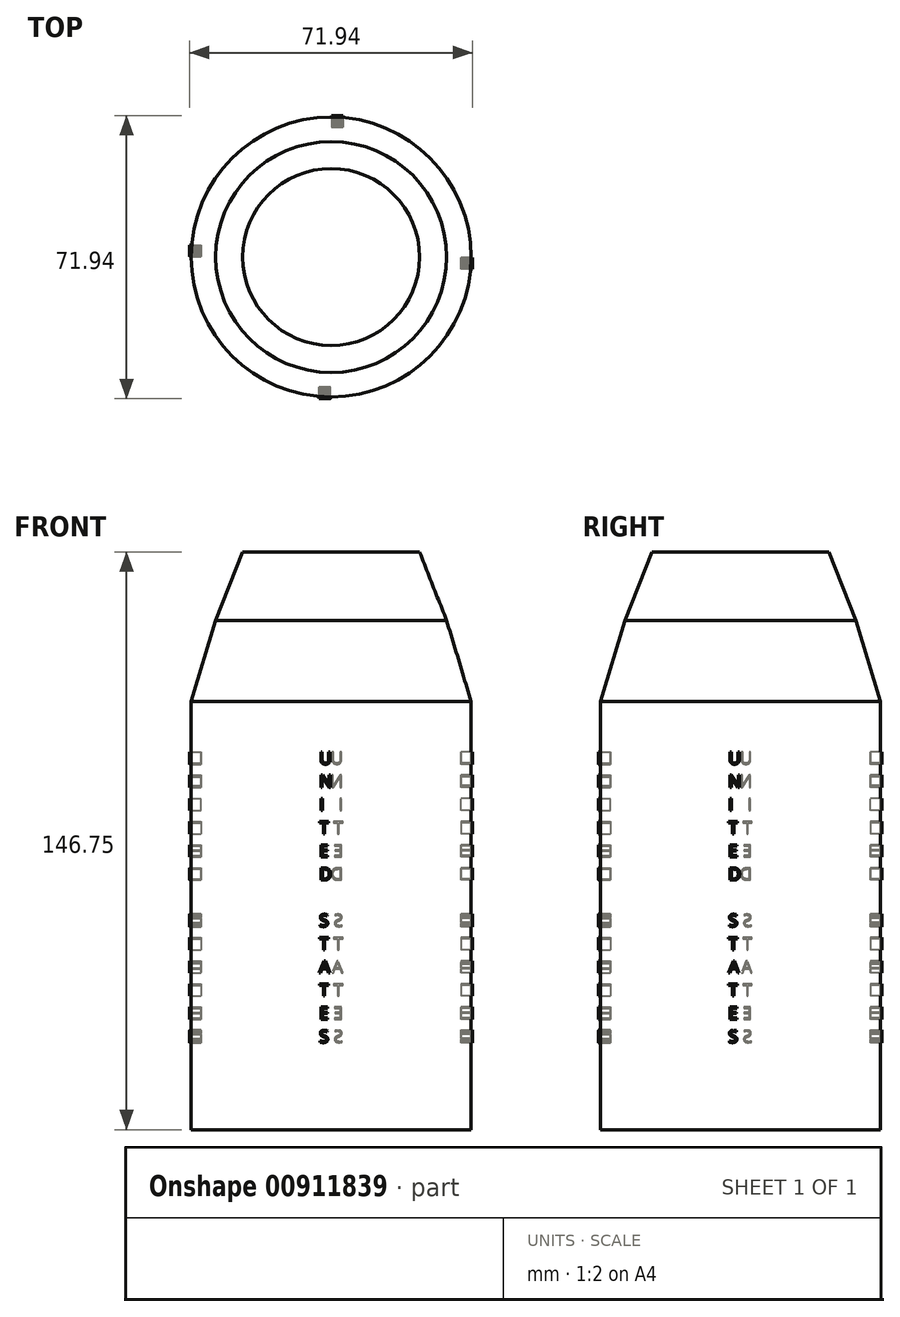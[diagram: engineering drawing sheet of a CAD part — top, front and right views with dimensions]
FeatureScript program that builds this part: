
annotation { "Feature Type Name" : "Feature", "Feature Type Description" : "" }
export const myFeature = defineFeature(function(context is Context, id is Id, definition is map)
    precondition{}
    {
        {
            var Q0;
            Q0=qCreatedBy(makeId("Front.planeOp"),FACE);
            var sketch = newSketch(context, id + "F0", { "sketchPlane" : qUnion([Q0])});
            skLineSegment(sketch, "E0.bottom", {"start": v(0, -75.35) * mm, "end": v(-35.56, -75.35) * mm});
            skLineSegment(sketch, "E0.top", {"start": v(0, 33.49) * mm, "end": v(-35.56, 33.49) * mm});
            skLineSegment(sketch, "E0.left", {"start": v(0, -75.35) * mm, "end": v(0, 33.49) * mm});
            skLineSegment(sketch, "E0.right", {"start": v(-35.56, -75.35) * mm, "end": v(-35.56, 33.49) * mm});
            skLineSegment(sketch, "E1", {"start": v(-35.56, 33.49) * mm, "end": v(-29.33, 53.99) * mm});
            skLineSegment(sketch, "E2", {"start": v(-29.33, 53.99) * mm, "end": v(0, 53.99) * mm});
            skLineSegment(sketch, "E3", {"start": v(0, 53.99) * mm, "end": v(0, 33.49) * mm});
            skLineSegment(sketch, "E4", {"start": v(-29.33, 53.99) * mm, "end": v(-22.49, 71.4) * mm});
            skLineSegment(sketch, "E5", {"start": v(0, 71.4) * mm, "end": v(0, 53.99) * mm});
            skLineSegment(sketch, "E6", {"start": v(0, 85.08) * mm, "end": v(0, -81.57) * mm});
            skLineSegment(sketch, "E7", {"start": v(-22.49, 71.4) * mm, "end": v(0, 71.4) * mm});
            skSolve(sketch);
        }
        {
            var Q0;
            Q0 = qSketchRegion(id + "F0", true);
            var Q1;
            Q1=sQuery(id+"F0.wireOp",EDGE,"E6");
            revolve(context, id + "F1", {"surfaceOperationType" : NewSurfaceOperationType.NEW, "entities" : qUnion([Q0]), "axis" : qUnion([Q1]), "revolveType" : RevolveType.FULL});
        }
        {
            var Q0;
            Q0=qCreatedBy(makeId("Front.planeOp"),FACE);
            cPlane(context, id + "F2", {"entities" : qUnion([Q0]), "cplaneType" : CPlaneType.OFFSET, "offset" : 33.02 * mm, "width" : 152.4 * mm, "height" : 152.4 * mm});
        }
        {
            var Q0;
            Q0=qCreatedBy(id+"F2.planeOp",FACE);
            var sketch = newSketch(context, id + "F3", { "sketchPlane" : qUnion([Q0])});
            skText(sketch, "E8", { "text": "U\nN\nI\nT\nE\nD\n\nS\nT\nA\nT\nE\nS", "fontName": "OpenSans-Regular.ttf"});
            const initialGuessF3  = {"E8": [-0.00302, 0.01752, 1, 0, 0.00312]};
            skSetInitialGuess(sketch, initialGuessF3);
            skSolve(sketch);
        }
        {
            var Q0;
            Q0 = qSketchRegion(id + "F3", true);
            extrude(context, id + "F4", {"entities" : qUnion([Q0]), "depth" : 2.95 * mm, "offsetDistance" : 25.4 * mm});
        }
        {
            var Q0;
            Q0=makeQuery(id+"F4.opExtrude","SWEPT_BODY",BODY,{"disambiguationData":[OSD([sQuery(id+"F3.wireOp",EDGE,"E8.sketch_text.stroke-0"),sQuery(id+"F3.wireOp",EDGE,"E8.sketch_text.stroke-1"),sQuery(id+"F3.wireOp",EDGE,"E8.sketch_text.stroke-2"),sQuery(id+"F3.wireOp",EDGE,"E8.sketch_text.stroke-3"),sQuery(id+"F3.wireOp",EDGE,"E8.sketch_text.stroke-4"),sQuery(id+"F3.wireOp",EDGE,"E8.sketch_text.stroke-5"),sQuery(id+"F3.wireOp",EDGE,"E8.sketch_text.stroke-6"),sQuery(id+"F3.wireOp",EDGE,"E8.sketch_text.stroke-7"),sQuery(id+"F3.wireOp",EDGE,"E8.sketch_text.stroke-8"),sQuery(id+"F3.wireOp",EDGE,"E8.sketch_text.stroke-9"),sQuery(id+"F3.wireOp",EDGE,"E8.sketch_text.stroke-10"),sQuery(id+"F3.wireOp",EDGE,"E8.sketch_text.stroke-11"),sQuery(id+"F3.wireOp",EDGE,"E8.sketch_text.stroke-12"),sQuery(id+"F3.wireOp",EDGE,"E8.sketch_text.stroke-13")])]});
            var Q1;
            Q1=makeQuery(id+"F4.opExtrude","SWEPT_BODY",BODY,{"disambiguationData":[OSD([sQuery(id+"F3.wireOp",EDGE,"E8.sketch_text.stroke-14"),sQuery(id+"F3.wireOp",EDGE,"E8.sketch_text.stroke-15"),sQuery(id+"F3.wireOp",EDGE,"E8.sketch_text.stroke-16"),sQuery(id+"F3.wireOp",EDGE,"E8.sketch_text.stroke-17"),sQuery(id+"F3.wireOp",EDGE,"E8.sketch_text.stroke-18"),sQuery(id+"F3.wireOp",EDGE,"E8.sketch_text.stroke-19"),sQuery(id+"F3.wireOp",EDGE,"E8.sketch_text.stroke-20"),sQuery(id+"F3.wireOp",EDGE,"E8.sketch_text.stroke-21"),sQuery(id+"F3.wireOp",EDGE,"E8.sketch_text.stroke-22"),sQuery(id+"F3.wireOp",EDGE,"E8.sketch_text.stroke-23"),sQuery(id+"F3.wireOp",EDGE,"E8.sketch_text.stroke-24"),sQuery(id+"F3.wireOp",EDGE,"E8.sketch_text.stroke-25"),sQuery(id+"F3.wireOp",EDGE,"E8.sketch_text.stroke-26"),sQuery(id+"F3.wireOp",EDGE,"E8.sketch_text.stroke-27"),sQuery(id+"F3.wireOp",EDGE,"E8.sketch_text.stroke-28")])]});
            var Q2;
            Q2=makeQuery(id+"F4.opExtrude","SWEPT_BODY",BODY,{"disambiguationData":[OSD([sQuery(id+"F3.wireOp",EDGE,"E8.sketch_text.stroke-29"),sQuery(id+"F3.wireOp",EDGE,"E8.sketch_text.stroke-30"),sQuery(id+"F3.wireOp",EDGE,"E8.sketch_text.stroke-31"),sQuery(id+"F3.wireOp",EDGE,"E8.sketch_text.stroke-32")])]});
            var Q3;
            Q3=makeQuery(id+"F4.opExtrude","SWEPT_BODY",BODY,{"disambiguationData":[OSD([sQuery(id+"F3.wireOp",EDGE,"E8.sketch_text.stroke-33"),sQuery(id+"F3.wireOp",EDGE,"E8.sketch_text.stroke-34"),sQuery(id+"F3.wireOp",EDGE,"E8.sketch_text.stroke-35"),sQuery(id+"F3.wireOp",EDGE,"E8.sketch_text.stroke-36"),sQuery(id+"F3.wireOp",EDGE,"E8.sketch_text.stroke-37"),sQuery(id+"F3.wireOp",EDGE,"E8.sketch_text.stroke-38"),sQuery(id+"F3.wireOp",EDGE,"E8.sketch_text.stroke-39"),sQuery(id+"F3.wireOp",EDGE,"E8.sketch_text.stroke-40")])]});
            var Q4;
            Q4=makeQuery(id+"F4.opExtrude","SWEPT_BODY",BODY,{"disambiguationData":[OSD([sQuery(id+"F3.wireOp",EDGE,"E8.sketch_text.stroke-41"),sQuery(id+"F3.wireOp",EDGE,"E8.sketch_text.stroke-42"),sQuery(id+"F3.wireOp",EDGE,"E8.sketch_text.stroke-43"),sQuery(id+"F3.wireOp",EDGE,"E8.sketch_text.stroke-44"),sQuery(id+"F3.wireOp",EDGE,"E8.sketch_text.stroke-45"),sQuery(id+"F3.wireOp",EDGE,"E8.sketch_text.stroke-46"),sQuery(id+"F3.wireOp",EDGE,"E8.sketch_text.stroke-47"),sQuery(id+"F3.wireOp",EDGE,"E8.sketch_text.stroke-48"),sQuery(id+"F3.wireOp",EDGE,"E8.sketch_text.stroke-49"),sQuery(id+"F3.wireOp",EDGE,"E8.sketch_text.stroke-50"),sQuery(id+"F3.wireOp",EDGE,"E8.sketch_text.stroke-51"),sQuery(id+"F3.wireOp",EDGE,"E8.sketch_text.stroke-52")])]});
            var Q5;
            Q5=makeQuery(id+"F4.opExtrude","SWEPT_BODY",BODY,{"disambiguationData":[OSD([sQuery(id+"F3.wireOp",EDGE,"E8.sketch_text.stroke-53"),sQuery(id+"F3.wireOp",EDGE,"E8.sketch_text.stroke-54"),sQuery(id+"F3.wireOp",EDGE,"E8.sketch_text.stroke-55"),sQuery(id+"F3.wireOp",EDGE,"E8.sketch_text.stroke-56"),sQuery(id+"F3.wireOp",EDGE,"E8.sketch_text.stroke-57"),sQuery(id+"F3.wireOp",EDGE,"E8.sketch_text.stroke-58"),sQuery(id+"F3.wireOp",EDGE,"E8.sketch_text.stroke-59"),sQuery(id+"F3.wireOp",EDGE,"E8.sketch_text.stroke-60"),sQuery(id+"F3.wireOp",EDGE,"E8.sketch_text.stroke-61"),sQuery(id+"F3.wireOp",EDGE,"E8.sketch_text.stroke-62"),sQuery(id+"F3.wireOp",EDGE,"E8.sketch_text.stroke-63"),sQuery(id+"F3.wireOp",EDGE,"E8.sketch_text.stroke-64"),sQuery(id+"F3.wireOp",EDGE,"E8.sketch_text.stroke-65"),sQuery(id+"F3.wireOp",EDGE,"E8.sketch_text.stroke-66")])]});
            var Q6;
            Q6=makeQuery(id+"F4.opExtrude","SWEPT_BODY",BODY,{"disambiguationData":[OSD([sQuery(id+"F3.wireOp",EDGE,"E8.sketch_text.stroke-67"),sQuery(id+"F3.wireOp",EDGE,"E8.sketch_text.stroke-68"),sQuery(id+"F3.wireOp",EDGE,"E8.sketch_text.stroke-69"),sQuery(id+"F3.wireOp",EDGE,"E8.sketch_text.stroke-70"),sQuery(id+"F3.wireOp",EDGE,"E8.sketch_text.stroke-71"),sQuery(id+"F3.wireOp",EDGE,"E8.sketch_text.stroke-72"),sQuery(id+"F3.wireOp",EDGE,"E8.sketch_text.stroke-73"),sQuery(id+"F3.wireOp",EDGE,"E8.sketch_text.stroke-74"),sQuery(id+"F3.wireOp",EDGE,"E8.sketch_text.stroke-75"),sQuery(id+"F3.wireOp",EDGE,"E8.sketch_text.stroke-76"),sQuery(id+"F3.wireOp",EDGE,"E8.sketch_text.stroke-77"),sQuery(id+"F3.wireOp",EDGE,"E8.sketch_text.stroke-78"),sQuery(id+"F3.wireOp",EDGE,"E8.sketch_text.stroke-79"),sQuery(id+"F3.wireOp",EDGE,"E8.sketch_text.stroke-80"),sQuery(id+"F3.wireOp",EDGE,"E8.sketch_text.stroke-81"),sQuery(id+"F3.wireOp",EDGE,"E8.sketch_text.stroke-82"),sQuery(id+"F3.wireOp",EDGE,"E8.sketch_text.stroke-83"),sQuery(id+"F3.wireOp",EDGE,"E8.sketch_text.stroke-84"),sQuery(id+"F3.wireOp",EDGE,"E8.sketch_text.stroke-85"),sQuery(id+"F3.wireOp",EDGE,"E8.sketch_text.stroke-86"),sQuery(id+"F3.wireOp",EDGE,"E8.sketch_text.stroke-87"),sQuery(id+"F3.wireOp",EDGE,"E8.sketch_text.stroke-88"),sQuery(id+"F3.wireOp",EDGE,"E8.sketch_text.stroke-89"),sQuery(id+"F3.wireOp",EDGE,"E8.sketch_text.stroke-90"),sQuery(id+"F3.wireOp",EDGE,"E8.sketch_text.stroke-91")])]});
            var Q7;
            Q7=makeQuery(id+"F4.opExtrude","SWEPT_BODY",BODY,{"disambiguationData":[OSD([sQuery(id+"F3.wireOp",EDGE,"E8.sketch_text.stroke-92"),sQuery(id+"F3.wireOp",EDGE,"E8.sketch_text.stroke-93"),sQuery(id+"F3.wireOp",EDGE,"E8.sketch_text.stroke-94"),sQuery(id+"F3.wireOp",EDGE,"E8.sketch_text.stroke-95"),sQuery(id+"F3.wireOp",EDGE,"E8.sketch_text.stroke-96"),sQuery(id+"F3.wireOp",EDGE,"E8.sketch_text.stroke-97"),sQuery(id+"F3.wireOp",EDGE,"E8.sketch_text.stroke-98"),sQuery(id+"F3.wireOp",EDGE,"E8.sketch_text.stroke-99")])]});
            var Q8;
            Q8=makeQuery(id+"F4.opExtrude","SWEPT_BODY",BODY,{"disambiguationData":[OSD([sQuery(id+"F3.wireOp",EDGE,"E8.sketch_text.stroke-100"),sQuery(id+"F3.wireOp",EDGE,"E8.sketch_text.stroke-101"),sQuery(id+"F3.wireOp",EDGE,"E8.sketch_text.stroke-102"),sQuery(id+"F3.wireOp",EDGE,"E8.sketch_text.stroke-103"),sQuery(id+"F3.wireOp",EDGE,"E8.sketch_text.stroke-104"),sQuery(id+"F3.wireOp",EDGE,"E8.sketch_text.stroke-105"),sQuery(id+"F3.wireOp",EDGE,"E8.sketch_text.stroke-106"),sQuery(id+"F3.wireOp",EDGE,"E8.sketch_text.stroke-107"),sQuery(id+"F3.wireOp",EDGE,"E8.sketch_text.stroke-108"),sQuery(id+"F3.wireOp",EDGE,"E8.sketch_text.stroke-109"),sQuery(id+"F3.wireOp",EDGE,"E8.sketch_text.stroke-110"),sQuery(id+"F3.wireOp",EDGE,"E8.sketch_text.stroke-111"),sQuery(id+"F3.wireOp",EDGE,"E8.sketch_text.stroke-112")])]});
            var Q9;
            Q9=makeQuery(id+"F4.opExtrude","SWEPT_BODY",BODY,{"disambiguationData":[OSD([sQuery(id+"F3.wireOp",EDGE,"E8.sketch_text.stroke-113"),sQuery(id+"F3.wireOp",EDGE,"E8.sketch_text.stroke-114"),sQuery(id+"F3.wireOp",EDGE,"E8.sketch_text.stroke-115"),sQuery(id+"F3.wireOp",EDGE,"E8.sketch_text.stroke-116"),sQuery(id+"F3.wireOp",EDGE,"E8.sketch_text.stroke-117"),sQuery(id+"F3.wireOp",EDGE,"E8.sketch_text.stroke-118"),sQuery(id+"F3.wireOp",EDGE,"E8.sketch_text.stroke-119"),sQuery(id+"F3.wireOp",EDGE,"E8.sketch_text.stroke-120")])]});
            var Q10;
            Q10=makeQuery(id+"F4.opExtrude","SWEPT_BODY",BODY,{"disambiguationData":[OSD([sQuery(id+"F3.wireOp",EDGE,"E8.sketch_text.stroke-121"),sQuery(id+"F3.wireOp",EDGE,"E8.sketch_text.stroke-122"),sQuery(id+"F3.wireOp",EDGE,"E8.sketch_text.stroke-123"),sQuery(id+"F3.wireOp",EDGE,"E8.sketch_text.stroke-124"),sQuery(id+"F3.wireOp",EDGE,"E8.sketch_text.stroke-125"),sQuery(id+"F3.wireOp",EDGE,"E8.sketch_text.stroke-126"),sQuery(id+"F3.wireOp",EDGE,"E8.sketch_text.stroke-127"),sQuery(id+"F3.wireOp",EDGE,"E8.sketch_text.stroke-128"),sQuery(id+"F3.wireOp",EDGE,"E8.sketch_text.stroke-129"),sQuery(id+"F3.wireOp",EDGE,"E8.sketch_text.stroke-130"),sQuery(id+"F3.wireOp",EDGE,"E8.sketch_text.stroke-131"),sQuery(id+"F3.wireOp",EDGE,"E8.sketch_text.stroke-132")])]});
            var Q11;
            Q11=makeQuery(id+"F4.opExtrude","SWEPT_BODY",BODY,{"disambiguationData":[OSD([sQuery(id+"F3.wireOp",EDGE,"E8.sketch_text.stroke-133"),sQuery(id+"F3.wireOp",EDGE,"E8.sketch_text.stroke-134"),sQuery(id+"F3.wireOp",EDGE,"E8.sketch_text.stroke-135"),sQuery(id+"F3.wireOp",EDGE,"E8.sketch_text.stroke-136"),sQuery(id+"F3.wireOp",EDGE,"E8.sketch_text.stroke-137"),sQuery(id+"F3.wireOp",EDGE,"E8.sketch_text.stroke-138"),sQuery(id+"F3.wireOp",EDGE,"E8.sketch_text.stroke-139"),sQuery(id+"F3.wireOp",EDGE,"E8.sketch_text.stroke-140"),sQuery(id+"F3.wireOp",EDGE,"E8.sketch_text.stroke-141"),sQuery(id+"F3.wireOp",EDGE,"E8.sketch_text.stroke-142"),sQuery(id+"F3.wireOp",EDGE,"E8.sketch_text.stroke-143"),sQuery(id+"F3.wireOp",EDGE,"E8.sketch_text.stroke-144"),sQuery(id+"F3.wireOp",EDGE,"E8.sketch_text.stroke-145"),sQuery(id+"F3.wireOp",EDGE,"E8.sketch_text.stroke-146"),sQuery(id+"F3.wireOp",EDGE,"E8.sketch_text.stroke-147"),sQuery(id+"F3.wireOp",EDGE,"E8.sketch_text.stroke-148"),sQuery(id+"F3.wireOp",EDGE,"E8.sketch_text.stroke-149"),sQuery(id+"F3.wireOp",EDGE,"E8.sketch_text.stroke-150"),sQuery(id+"F3.wireOp",EDGE,"E8.sketch_text.stroke-151"),sQuery(id+"F3.wireOp",EDGE,"E8.sketch_text.stroke-152"),sQuery(id+"F3.wireOp",EDGE,"E8.sketch_text.stroke-153"),sQuery(id+"F3.wireOp",EDGE,"E8.sketch_text.stroke-154"),sQuery(id+"F3.wireOp",EDGE,"E8.sketch_text.stroke-155"),sQuery(id+"F3.wireOp",EDGE,"E8.sketch_text.stroke-156"),sQuery(id+"F3.wireOp",EDGE,"E8.sketch_text.stroke-157")])]});
            var Q12;
            Q12=makeQuery(id+"F1.opRevolve","SWEPT_EDGE",EDGE,{"disambiguationData":[OSD([sQuery(id+"F0.wireOp",EDGE,"E4"),sQuery(id+"F0.wireOp",EDGE,"E7")])]});
            circularPattern(context, id + "F5", {"entities" : qUnion([Q0, Q1, Q2, Q3, Q4, Q5, Q6, Q7, Q8, Q9, Q10, Q11]), "axis" : qUnion([Q12]), "angle" : 360 * degree, "instanceCount" : 4, "equalSpace" : true});
        }
    });
